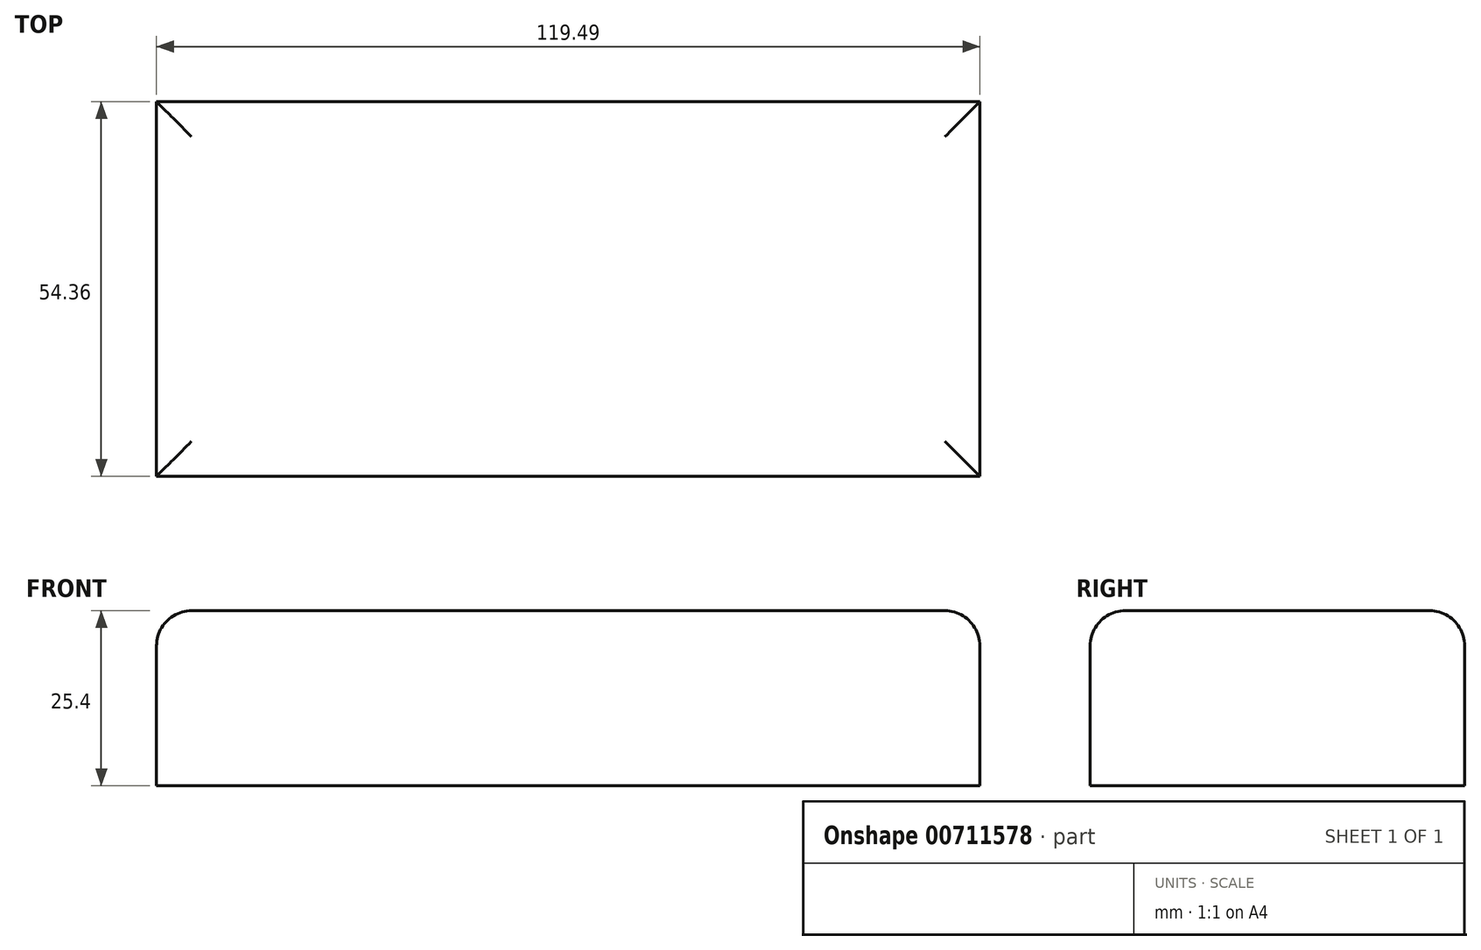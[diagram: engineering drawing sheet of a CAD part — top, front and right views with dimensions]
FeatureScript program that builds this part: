
annotation { "Feature Type Name" : "Feature", "Feature Type Description" : "" }
export const myFeature = defineFeature(function(context is Context, id is Id, definition is map)
    precondition{}
    {
        {
            var Q0;
            Q0=qCreatedBy(makeId("Top.planeOp"),FACE);
            var sketch = newSketch(context, id + "F0", { "sketchPlane" : qUnion([Q0])});
            skLineSegment(sketch, "E0.bottom", {"start": v(0, 0) * mm, "end": v(119.49, 0) * mm});
            skLineSegment(sketch, "E0.top", {"start": v(0, -54.36) * mm, "end": v(119.49, -54.36) * mm});
            skLineSegment(sketch, "E0.left", {"start": v(0, 0) * mm, "end": v(0, -54.36) * mm});
            skLineSegment(sketch, "E0.right", {"start": v(119.49, 0) * mm, "end": v(119.49, -54.36) * mm});
            skSolve(sketch);
        }
        {
            var Q0;
            Q0 = qSketchRegion(id + "F0", true);
            extrude(context, id + "F1", {"entities" : qUnion([Q0]), "depth" : 25.4 * mm, "offsetDistance" : 25.4 * mm});
        }
        {
            var Q0;
            Q0=makeQuery(id+"F1.opExtrude","CAP_EDGE",EDGE,{"disambiguationData":[OSD([sQuery(id+"F0.wireOp",EDGE,"E0.left")])],"isStart":false});
            var Q1;
            Q1=makeQuery(id+"F1.opExtrude","CAP_EDGE",EDGE,{"disambiguationData":[OSD([sQuery(id+"F0.wireOp",EDGE,"E0.right")])],"isStart":false});
            var Q2;
            Q2=makeQuery(id+"F1.opExtrude","CAP_EDGE",EDGE,{"disambiguationData":[OSD([sQuery(id+"F0.wireOp",EDGE,"E0.top")])],"isStart":false});
            var Q3;
            Q3=makeQuery(id+"F1.opExtrude","CAP_EDGE",EDGE,{"disambiguationData":[OSD([sQuery(id+"F0.wireOp",EDGE,"E0.bottom")])],"isStart":false});
            fillet(context, id + "F2", {"entities" : qUnion([Q0, Q1, Q2, Q3]), "radius" : 5.08 * mm, "tangentPropagation" : true, "allowEdgeOverflow" : false});
        }
    });
